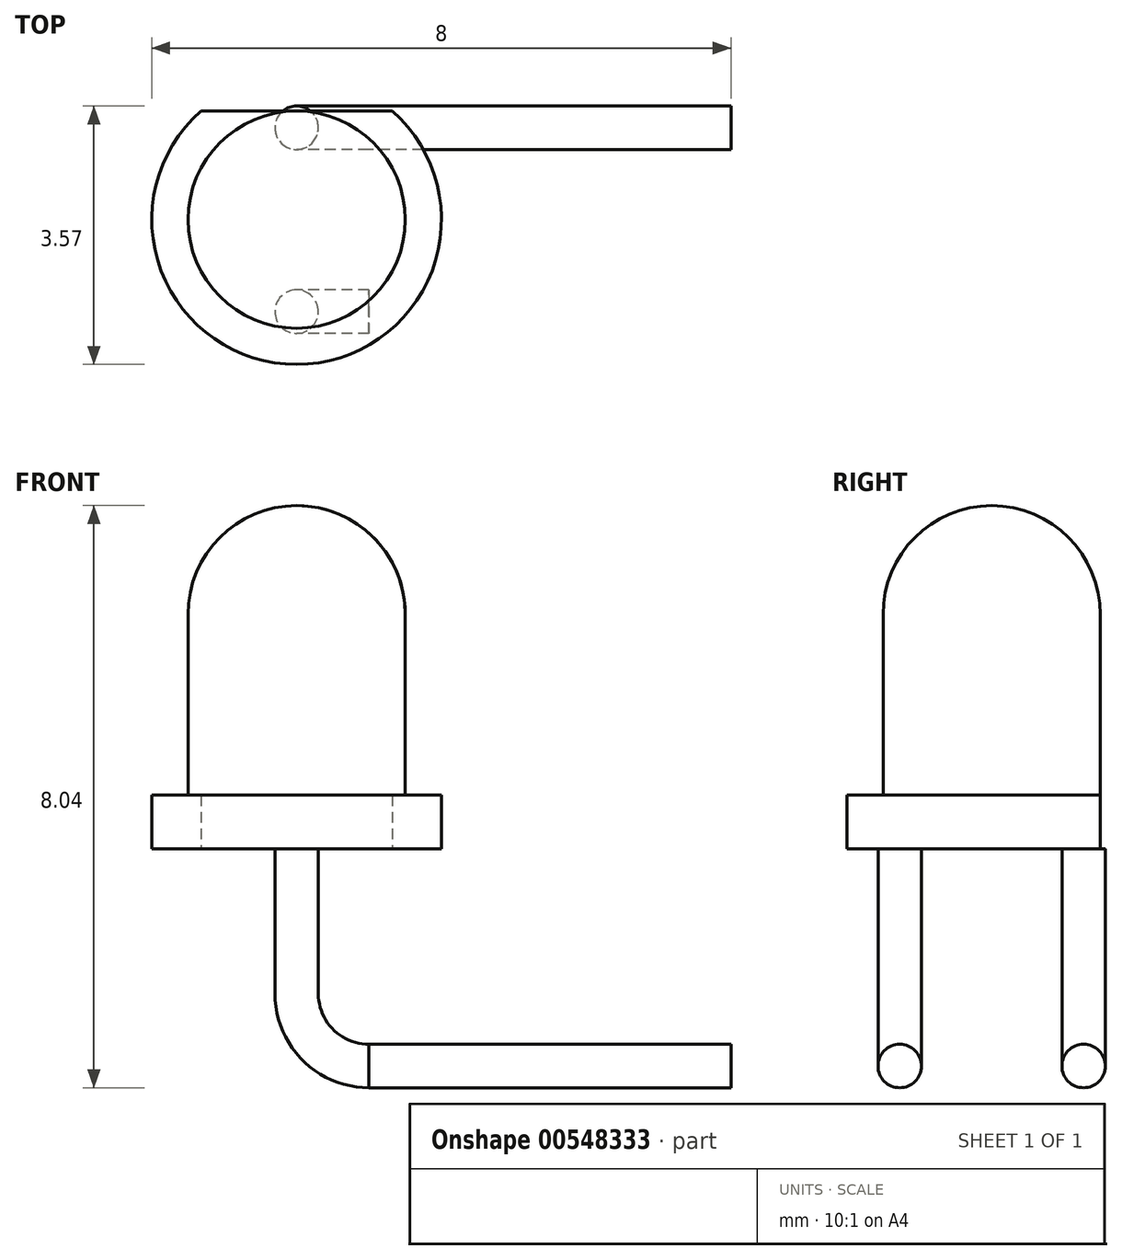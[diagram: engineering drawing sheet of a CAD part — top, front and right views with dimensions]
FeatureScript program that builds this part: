
annotation { "Feature Type Name" : "Feature", "Feature Type Description" : "" }
export const myFeature = defineFeature(function(context is Context, id is Id, definition is map)
    precondition{}
    {
        {
            var Q0;
            Q0=qCreatedBy(makeId("Front.planeOp"),FACE);
            var sketch = newSketch(context, id + "F0", { "sketchPlane" : qUnion([Q0])});
            skLineSegment(sketch, "E0", {"start": v(0, 0) * mm, "end": v(0, 4) * mm});
            skLineSegment(sketch, "E1", {"start": v(0, 0) * mm, "end": v(1.5, 0) * mm, "construction": true});
            skLineSegment(sketch, "E2", {"start": v(1.5, 0) * mm, "end": v(1.5, 2.5) * mm});
            skArc(sketch, "E3", {"start": v(0, 4) * mm, "mid": v(1.06, 3.56) * mm, "end": v(1.5, 2.5) * mm});
            skLineSegment(sketch, "E4", {"start": v(1.5, 2.5) * mm, "end": v(0, 2.5) * mm, "construction": true});
            skLineSegment(sketch, "E5", {"start": v(1.5, 0) * mm, "end": v(2, 0) * mm});
            skLineSegment(sketch, "E6", {"start": v(2, 0) * mm, "end": v(2, -0.74) * mm});
            skLineSegment(sketch, "E7", {"start": v(2, -0.74) * mm, "end": v(0, -0.74) * mm});
            skLineSegment(sketch, "E8", {"start": v(0, -0.74) * mm, "end": v(0, 0) * mm});
            skSolve(sketch);
        }
        {
            var Q0;
            Q0 = qSketchRegion(id + "F0", true);
            var Q1;
            Q1=sQuery(id+"F0.wireOp",EDGE,"E0");
            revolve(context, id + "F1", {"entities" : qUnion([Q0]), "axis" : qUnion([Q1]), "revolveType" : RevolveType.FULL});
        }
        {
            var Q0;
            Q0=makeQuery(id+"F1.opRevolve","SWEPT_FACE",FACE,{"disambiguationData":[OSD([sQuery(id+"F0.wireOp",EDGE,"E7")])]});
            var sketch = newSketch(context, id + "F2", { "sketchPlane" : qUnion([Q0])});
            skCircle(sketch, "E9", {"center": v(0, 0) * mm, "radius": 2 * mm});
            skLineSegment(sketch, "E10", {"start": v(1.32, -1.5) * mm, "end": v(-1.32, -1.5) * mm});
            skSolve(sketch);
        }
        {
            var Q0;
            {var subQ0=sQuery(id+"F2.wireOp",EDGE,"E10");Q0=makeQuery(id+"F2.imprint","IMPRINT",FACE,{"disambiguationData":[TD([[makeQuery(id+"F2.imprint","IMPRINT",EDGE,{"derivedFrom":subQ0}),1.0]])]});}
            extrude(context, id + "F3", {"entities" : qUnion([Q0]), "operationType" : NewBodyOperationType.REMOVE, "oppositeDirection" : true, "depth" : 25 * mm, "offsetDistance" : 25 * mm});
        }
        {
            var Q0;
            Q0=makeQuery(id+"F1.opRevolve","SWEPT_FACE",FACE,{"disambiguationData":[OSD([sQuery(id+"F0.wireOp",EDGE,"E7")])]});
            var sketch = newSketch(context, id + "F4", { "sketchPlane" : qUnion([Q0])});
            skCircle(sketch, "E11", {"center": v(0, 1.27) * mm, "radius": 0.3 * mm});
            skCircle(sketch, "E12", {"center": v(0, -1.27) * mm, "radius": 0.3 * mm});
            skLineSegment(sketch, "E13", {"start": v(0, 0) * mm, "end": v(0, 1.27) * mm});
            skLineSegment(sketch, "E14", {"start": v(0, 0) * mm, "end": v(0, -1.27) * mm});
            skSolve(sketch);
        }
        {
            var Q0;
            Q0 = qSketchRegion(id + "F4", true);
            extrude(context, id + "F5", {"entities" : qUnion([Q0]), "operationType" : NewBodyOperationType.ADD, "depth" : 2 * mm, "offsetDistance" : 25 * mm});
        }
        {
            var Q0;
            Q0=makeQuery(id+"F5.opExtrude","CAP_FACE",FACE,{"disambiguationData":[OSD([sQuery(id+"F4.wireOp",EDGE,"E12")])],"isStart":false});
            var sketch = newSketch(context, id + "F6", { "sketchPlane" : qUnion([Q0])});
            skLineSegment(sketch, "E15", {"start": v(1, -1.78) * mm, "end": v(1, 1.23) * mm, "construction": true});
            skSolve(sketch);
        }
        {
            var Q0;
            Q0=makeQuery(id+"F5.opExtrude","CAP_FACE",FACE,{"disambiguationData":[OSD([sQuery(id+"F4.wireOp",EDGE,"E11")])],"isStart":false});
            var Q1;
            Q1=makeQuery(id+"F6.imprint","IMPRINT",FACE,{"disambiguationData":[TD([[makeQuery(id+"F6.imprint","IMPRINT",EDGE,{"derivedFrom":makeQuery(id+"F5.opExtrude","CAP_EDGE",EDGE,{"disambiguationData":[OSD([sQuery(id+"F4.wireOp",EDGE,"E12")])],"isStart":false})}),1.0]])]});
            var Q2;
            Q2=sQuery(id+"F6.wireOp",EDGE,"E15");
            revolve(context, id + "F7", {"operationType" : NewBodyOperationType.ADD, "entities" : qUnion([Q0, Q1]), "axis" : qUnion([Q2]), "revolveType" : RevolveType.ONE_DIRECTION, "angle" : 90 * degree});
        }
        {
            var Q0;
            Q0=makeQuery(id+"F7.opRevolve","CAP_FACE",FACE,{"disambiguationData":[OSD([sQuery(id+"F4.wireOp",EDGE,"E11")])],"isStart":false});
            var sketch = newSketch(context, id + "F8", { "sketchPlane" : qUnion([Q0])});
            skSolve(sketch);
        }
        {
            var Q0;
            Q0=makeQuery(id+"F8.imprint","IMPRINT",FACE,{"disambiguationData":[TD([[makeQuery(id+"F8.imprint","IMPRINT",EDGE,{"derivedFrom":makeQuery(id+"F7.opRevolve","CAP_EDGE",EDGE,{"disambiguationData":[OSD([sQuery(id+"F4.wireOp",EDGE,"E11")])],"isStart":false})}),1.0]])]});
            var Q1;
            Q1=makeQuery(id+"F7.opRevolve","CAP_FACE",FACE,{"disambiguationData":[OSD([sQuery(id+"F4.wireOp",EDGE,"E12")])],"isStart":false});
            extrude(context, id + "F9", {"entities" : qUnion([Q0, Q1]), "operationType" : NewBodyOperationType.ADD, "depth" : 5 * mm, "offsetDistance" : 25 * mm});
        }
    });
